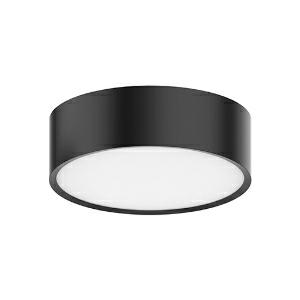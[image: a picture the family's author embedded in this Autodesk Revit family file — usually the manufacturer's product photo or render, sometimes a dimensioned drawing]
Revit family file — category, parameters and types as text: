
# Revit family: ledceilinglu-e_rd142-18w-830-bl_540001295900
name_source: partatom
category: Leuchten
revit_build: Autodesk Revit 2016 (Build: 20190508_0715(x64)
units: mm (PartAtom-declared; Revit-internal decimal feet)

## family parameters
Basisbauteil = Fläche
Beim Laden mit Abzugskörper schneiden = Nein
Bemaßung runder Anschluss = Durchmesser verwenden
Gemeinsam genutzt = Nein
Lichtquelle = Nein
Raumberechnungspunkt = Nein
Teiletyp = Normal

## types (1)
- LEDCeilingLu-E Rd142-18W-830-BL (1 x LED, 1620 lm)
    Approval mark = CE
    Beschreibung = Stylish and compact ceiling luminaire. Clean “twist-and-lock” mounting system. High quality full metal body. Low height of only 46mm. Suitable for ceiling and wall mounting.
    CIE Flux Codes = 49 79 96 100 100
    Control Gear = Electronic ballast
    Height = 100 mm  [stored 0.328084 ft]
    Hersteller = OPPLE
    Lamp Light Flux = 1620 lm
    Lamp count = 1
    Lampe = 1 x LED
    Length = 100 mm  [stored 0.328084 ft]
    Luminous efficacy = 90 lm/W
    ModVariant = Nein
    Modell = 540001295900
    Mounting Place = Wall, Ceiling
    Mounting Type = Surface mounted
    Number of Poles = 1
    OnlyDefault = Ja
    Power Factor = 1
    Product Name = LEDCeilingLu-E Rd142-18W-830-BL
    Product group = Ceiling Light Luna
    ProductGroupID = 305
    Protection Class = Protection class II
    Protection Degree = IP 20
    RLX_Detail_Level = 1
    RlxData = <blob elided: 129673 chars, md5=42df53fd>
    Scheinlast = 18 VA
    Socket = socket
    Standby Power = 0 W
    System Light Flux = 1620 lm
    System Power = 18 W
    Typenbild = luna_bl_rd142.jpg
    Typenkommentare = Product without accessories
    URL = http://relux.com
    VarID = ---
    Voltage = 230 V
    Voltage Range = 220-240 V
    Vorgabe-Ansicht = 1800 mm
    Weight = 0.00 kg
    Width = 100 mm  [stored 0.328084 ft]

note: [stored X ft] marks values corroborated as IEEE doubles in the binary element streams (Revit-internal decimal feet)

## geometry (parser evidence)
native form markers: Blend x4, Sweep x13
no freeform markers — native parametric forms only
